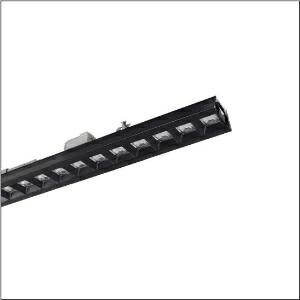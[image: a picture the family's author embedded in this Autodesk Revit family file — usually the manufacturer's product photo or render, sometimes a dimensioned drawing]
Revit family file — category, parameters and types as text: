
# Revit family: licross_21_silica_51ts12dn4zm00582xx
name_source: partatom
category: Lighting Fixtures
units: mm (PartAtom-declared; Revit-internal decimal feet)

## family parameters
Cut with Voids When Loaded = No
Host = Face
Light Source = No
Part Type = Normal
Room Calculation Point = No
Round Connector Dimension = Use Diameter
Shared = No

## types (1)
- --- (1 x LED, 6340 lm, 39 W, 4000K)
    Apparent Load = 39 VA
    CIE Flux Codes = 86 100 100 100 100
    Color Rendering = 80
    Color Temperature = 4000K
    Default Elevation = 1800 mm
    Description = Licross 21 Silica, luminaire insert, of sheet steel, galvanised, black, length: 1.500mm, width: 82mm, height: 86mm, LED rated luminous flux: 6.340lm, light colour: 840, SDCM (Standard Deviation of Colour Matching)MacAdam ≤ 3 SDCM (initial), control gear: DALI 2, with plug, 5-pole, with phase selection, mains connection: 220..240V, AC, 50/60Hz, rated input power: 39W, internal wiring halogen-free, primary light control with lens, of PMMA, primary anti-glare with darklight reflector, of PC, CAT 2 (L<= 1000cd/m²), light emission: direct distribution, primary light characteristic: symmetric, protection rating (complete): IP40, insulation class (complete): insulation class I (protective earthing), certification: CE, UKCA, protection symbol: D if used in an environment without relevant dust loads, impact resistance: IK03, permissible ambient temperature for indoor applications: -25..+45°C, corresponds to IFS (International Featured Standards) requirements for safety and quality in the food industry, reducing of maximum allowable ambient temperature of 5°C with ceiling mounting, LABS conformity tested according to VDMA 24364:2018-05, packaging unit: 1 piece
    Height = 86 mm
    Lamp = 1 x LED
    Lamp Light Flux = 6340 lm
    Lamp Power = 39 W
    Lamp count = 1
    Length = 1500 mm
    Luminous efficacy = 163 lm/W
    Manufacturer = Siteco
    ModVariant = No
    Model = 51TS12DN4ZM00582XX
    Mounting Place = Ceiling
    Mounting Type = Pendant
    Number of Poles = 1
    OnlyDefault = Yes
    Power Factor = 1
    Product Name = Licross 21 Silica
    Product group = luminaire insert | ceiling pendant
    ProductGroupID = 901
    Protection Class = Protection class I
    Protection Degree = IP 40
    RLX_Detail_Level = 1
    RLX_Emergency_Light_Flux = 0 lm
    RLX_Emergency_Type = 0
    RLX_Emergency_Type_DB = No
    RlxData = <blob elided: 56293 chars, md5=6df25932>
    Socket = socket
    Standby Power = 0 W
    System Light Flux = 6340 lm
    System Power = 39 W
    Type Comments = factory setting: luminous flux: 100 % | dim-lin: 254 | 435 mA
    Type Image = l_1290829.jpg
    URL = http://relux.com
    VarID = @adj_107937
    Voltage = 0 V
    Weight = 0.00 kg
    Width = 82 mm  [stored 0.269029 ft]

note: [stored X ft] marks values corroborated as IEEE doubles in the binary element streams (Revit-internal decimal feet)

## geometry (parser evidence)
native form markers: Blend x4, Sweep x11
no freeform markers — native parametric forms only
